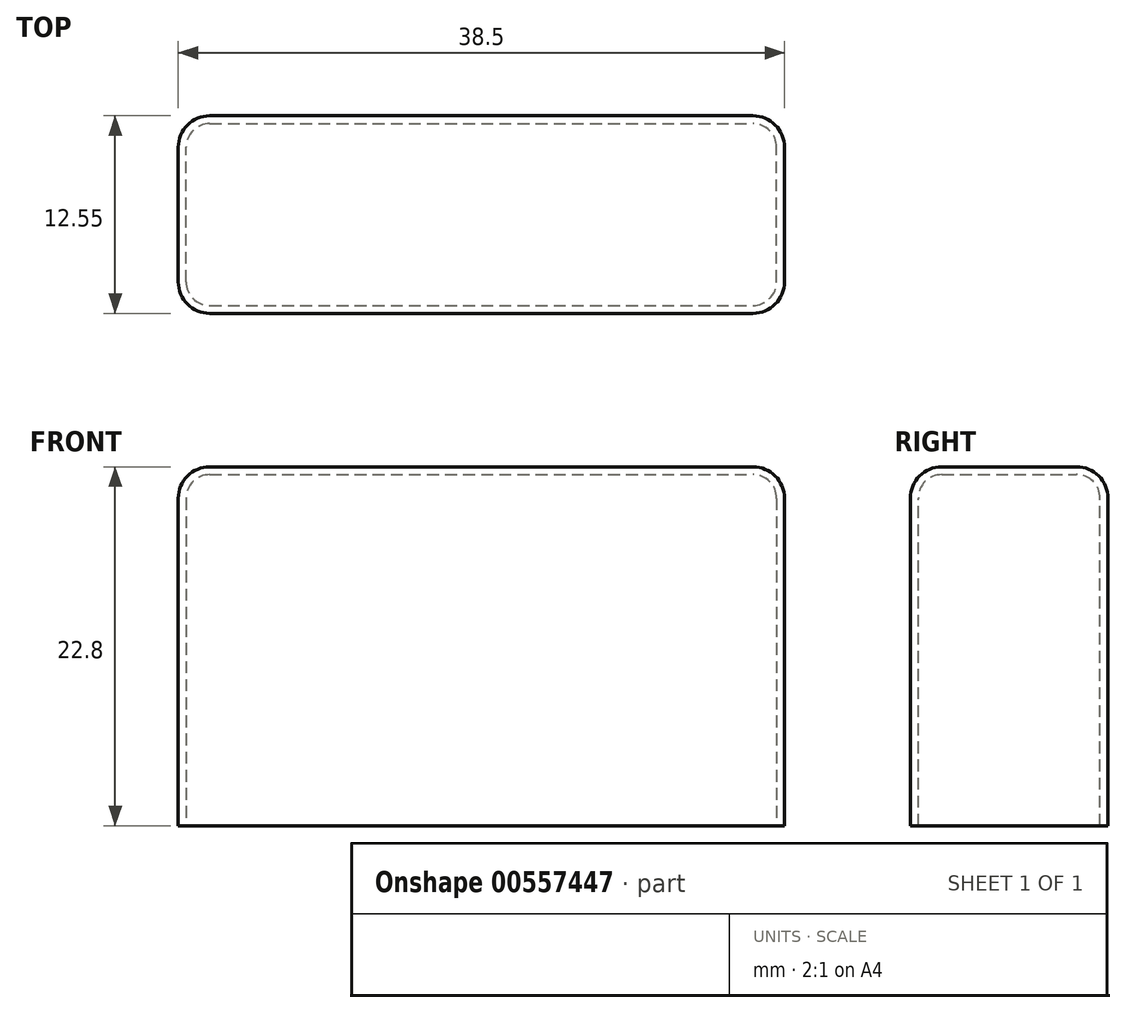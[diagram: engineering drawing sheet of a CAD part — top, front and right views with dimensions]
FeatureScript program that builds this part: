
annotation { "Feature Type Name" : "Feature", "Feature Type Description" : "" }
export const myFeature = defineFeature(function(context is Context, id is Id, definition is map)
    precondition{}
    {
        {
            var Q0;
            Q0=qCreatedBy(makeId("Front.planeOp"),FACE);
            var sketch = newSketch(context, id + "F0", { "sketchPlane" : qUnion([Q0])});
            skLineSegment(sketch, "E0.bottom", {"start": v(-45.6, 31.7) * mm, "end": v(-7.1, 31.7) * mm});
            skLineSegment(sketch, "E0.top", {"start": v(-45.6, 8.9) * mm, "end": v(-7.1, 8.9) * mm});
            skLineSegment(sketch, "E0.left", {"start": v(-45.6, 31.7) * mm, "end": v(-45.6, 8.9) * mm});
            skLineSegment(sketch, "E0.right", {"start": v(-7.1, 31.7) * mm, "end": v(-7.1, 8.9) * mm});
            skSolve(sketch);
        }
        {
            var Q0;
            Q0=makeQuery(id+"F0.imprint","IMPRINT",FACE,{"disambiguationData":[TD([[makeQuery(id+"F0.imprint","IMPRINT",EDGE,{"derivedFrom":sQuery(id+"F0.wireOp",EDGE,"E0.bottom")}),-1.0]])]});
            extrude(context, id + "F1", {"entities" : qUnion([Q0]), "depth" : 12.55 * mm, "offsetDistance" : 25 * mm});
        }
        {
            var Q0;
            Q0=makeQuery(id+"F1.opExtrude","CAP_EDGE",EDGE,{"disambiguationData":[OSD([sQuery(id+"F0.wireOp",EDGE,"E0.left")])],"isStart":false});
            var Q1;
            Q1=makeQuery(id+"F1.opExtrude","CAP_EDGE",EDGE,{"disambiguationData":[OSD([sQuery(id+"F0.wireOp",EDGE,"E0.left")])],"isStart":true});
            var Q2;
            Q2=makeQuery(id+"F1.opExtrude","CAP_EDGE",EDGE,{"disambiguationData":[OSD([sQuery(id+"F0.wireOp",EDGE,"E0.right")])],"isStart":false});
            var Q3;
            Q3=makeQuery(id+"F1.opExtrude","CAP_EDGE",EDGE,{"disambiguationData":[OSD([sQuery(id+"F0.wireOp",EDGE,"E0.right")])],"isStart":true});
            var Q4;
            Q4=makeQuery(id+"F1.opExtrude","CAP_EDGE",EDGE,{"disambiguationData":[OSD([sQuery(id+"F0.wireOp",EDGE,"E0.bottom")])],"isStart":false});
            var Q5;
            Q5=makeQuery(id+"F1.opExtrude","SWEPT_EDGE",EDGE,{"disambiguationData":[OSD([sQuery(id+"F0.wireOp",EDGE,"E0.bottom"),sQuery(id+"F0.wireOp",EDGE,"E0.right")])]});
            var Q6;
            Q6=makeQuery(id+"F1.opExtrude","CAP_EDGE",EDGE,{"disambiguationData":[OSD([sQuery(id+"F0.wireOp",EDGE,"E0.bottom")])],"isStart":true});
            var Q7;
            Q7=makeQuery(id+"F1.opExtrude","SWEPT_EDGE",EDGE,{"disambiguationData":[OSD([sQuery(id+"F0.wireOp",EDGE,"E0.bottom"),sQuery(id+"F0.wireOp",EDGE,"E0.left")])]});
            fillet(context, id + "F2", {"entities" : qUnion([Q0, Q1, Q2, Q3, Q4, Q5, Q6, Q7]), "tangentPropagation" : true, "radius" : 2 * mm, "defaultsChanged" : false, "vertexSettings" : [], "allowEdgeOverflow" : false});
        }
        {
            var Q0;
            Q0=makeQuery(id+"F1.opExtrude","SWEPT_FACE",FACE,{"disambiguationData":[OSD([sQuery(id+"F0.wireOp",EDGE,"E0.top")])]});
            shell(context, id + "F3", {"entities" : qUnion([Q0]), "thickness" : 0.5 * mm});
        }
    });
